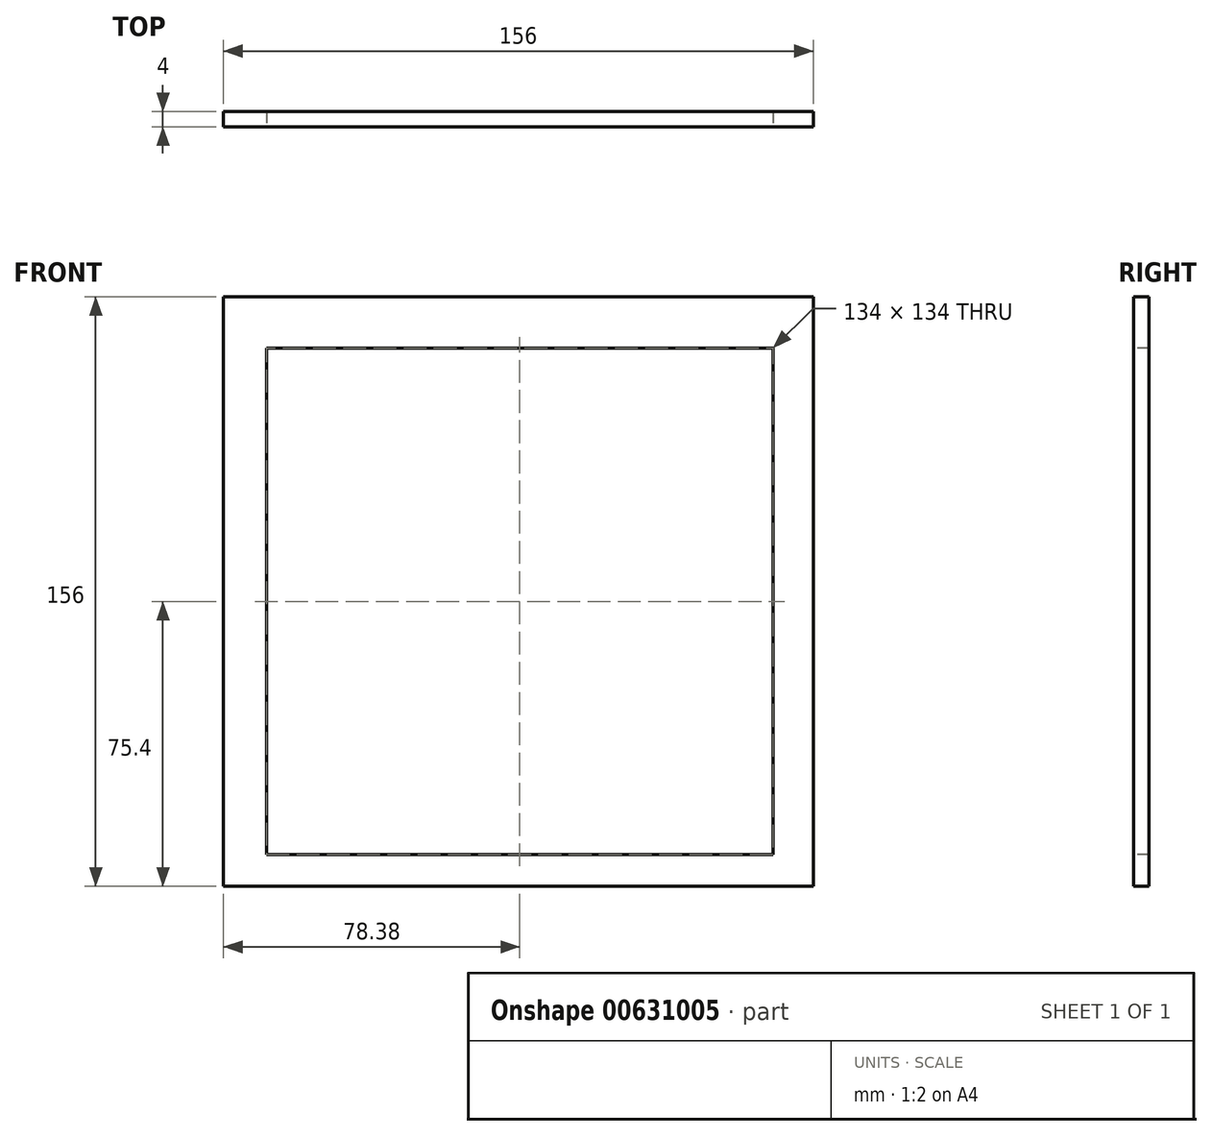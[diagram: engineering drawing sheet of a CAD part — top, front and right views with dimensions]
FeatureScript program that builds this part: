
annotation { "Feature Type Name" : "Feature", "Feature Type Description" : "" }
export const myFeature = defineFeature(function(context is Context, id is Id, definition is map)
    precondition{}
    {
        {
            var Q0;
            Q0=qCreatedBy(makeId("Front.planeOp"),FACE);
            var sketch = newSketch(context, id + "F0", { "sketchPlane" : qUnion([Q0])});
            skLineSegment(sketch, "E0.bottom", {"start": v(-78.38, 80.6) * mm, "end": v(77.62, 80.6) * mm});
            skLineSegment(sketch, "E0.top", {"start": v(-78.38, -75.4) * mm, "end": v(77.62, -75.4) * mm});
            skLineSegment(sketch, "E0.left", {"start": v(-78.38, 80.6) * mm, "end": v(-78.38, -75.4) * mm});
            skLineSegment(sketch, "E0.right", {"start": v(77.62, 80.6) * mm, "end": v(77.62, -75.4) * mm});
            skSolve(sketch);
        }
        {
            var Q0;
            Q0=makeQuery(id+"F0.imprint","IMPRINT",FACE,{"disambiguationData":[TD([[makeQuery(id+"F0.imprint","IMPRINT",EDGE,{"derivedFrom":sQuery(id+"F0.wireOp",EDGE,"E0.bottom")}),-1.0]])]});
            extrude(context, id + "F1", {"entities" : qUnion([Q0]), "depth" : 4 * mm, "offsetDistance" : 25 * mm});
        }
        {
            var Q0;
            Q0=makeQuery(id+"F1.opExtrude","CAP_FACE",FACE,{"disambiguationData":[OSD([sQuery(id+"F0.wireOp",EDGE,"E0.bottom"),sQuery(id+"F0.wireOp",EDGE,"E0.top"),sQuery(id+"F0.wireOp",EDGE,"E0.left"),sQuery(id+"F0.wireOp",EDGE,"E0.right")])],"isStart":false});
            var sketch = newSketch(context, id + "F2", { "sketchPlane" : qUnion([Q0])});
            skLineSegment(sketch, "E1.bottom", {"start": v(67, 67) * mm, "end": v(-67, 67) * mm});
            skLineSegment(sketch, "E1.top", {"start": v(67, -67) * mm, "end": v(-67, -67) * mm});
            skLineSegment(sketch, "E1.left", {"start": v(67, 67) * mm, "end": v(67, -67) * mm});
            skLineSegment(sketch, "E1.right", {"start": v(-67, 67) * mm, "end": v(-67, -67) * mm});
            skPoint(sketch, "E1.middle", {"position": v(0, 0) * mm});
            skSolve(sketch);
        }
        {
            var Q0;
            Q0=makeQuery(id+"F2.imprint","IMPRINT",FACE,{"disambiguationData":[TD([[makeQuery(id+"F2.imprint","IMPRINT",EDGE,{"derivedFrom":sQuery(id+"F2.wireOp",EDGE,"E1.bottom")}),1.0]])]});
            extrude(context, id + "F3", {"entities" : qUnion([Q0]), "operationType" : NewBodyOperationType.REMOVE, "oppositeDirection" : true, "depth" : 4 * mm, "offsetDistance" : 25 * mm});
        }
    });
